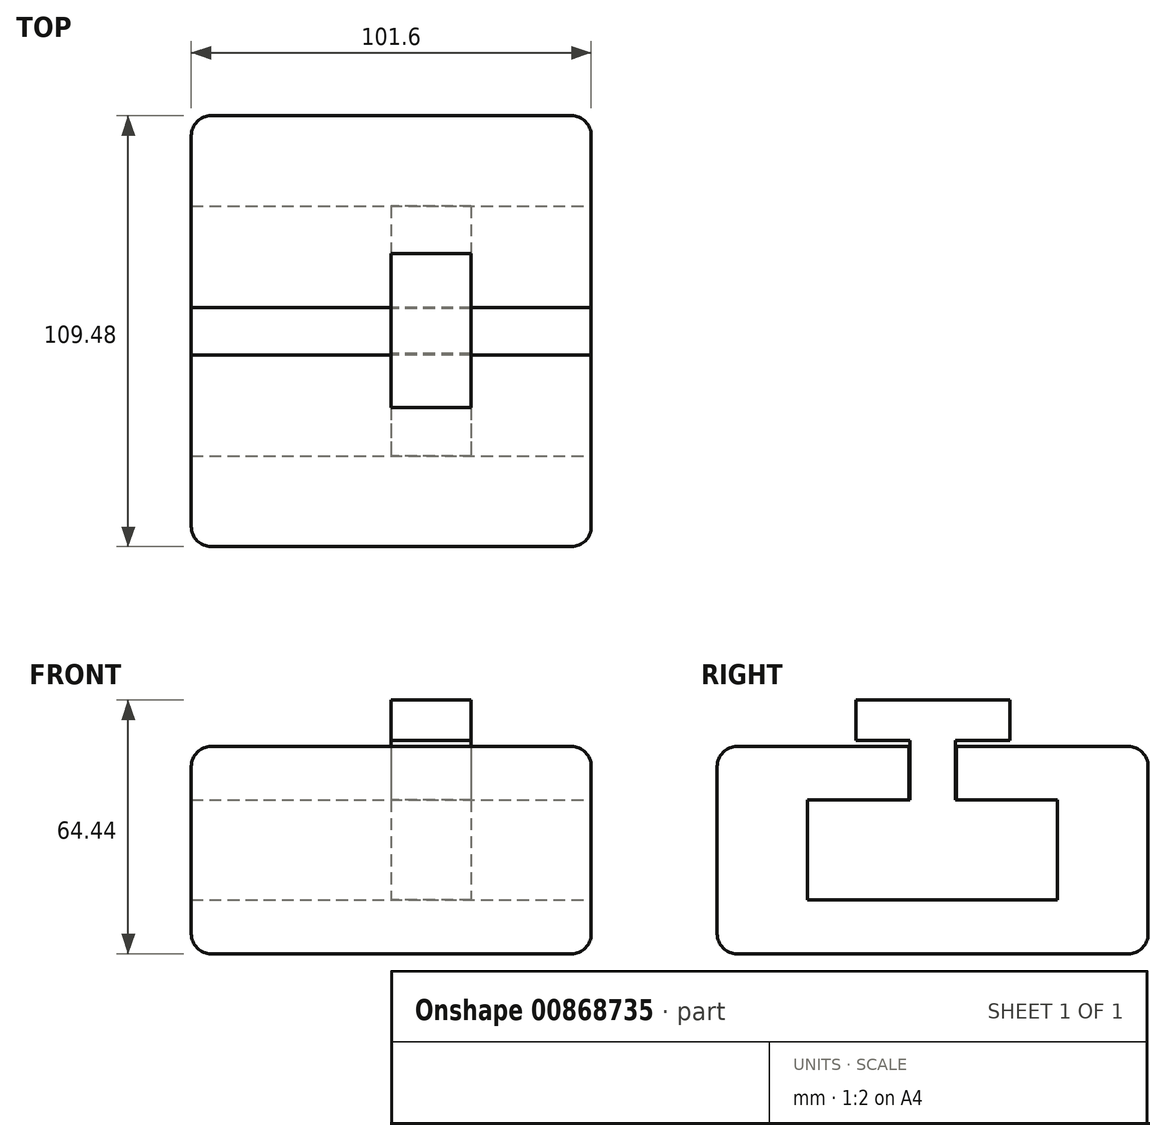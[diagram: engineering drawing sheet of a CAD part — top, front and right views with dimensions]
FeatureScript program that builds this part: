
annotation { "Feature Type Name" : "Feature", "Feature Type Description" : "" }
export const myFeature = defineFeature(function(context is Context, id is Id, definition is map)
    precondition{}
    {
        {
            var Q0;
            Q0=qCreatedBy(makeId("Right.planeOp"),FACE);
            var sketch = newSketch(context, id + "F0", { "sketchPlane" : qUnion([Q0])});
            skLineSegment(sketch, "E0.bottom", {"start": v(54.74, 26.34) * mm, "end": v(-54.74, 26.34) * mm});
            skLineSegment(sketch, "E0.top", {"start": v(54.74, -26.34) * mm, "end": v(-54.74, -26.34) * mm});
            skLineSegment(sketch, "E0.left", {"start": v(54.74, 26.34) * mm, "end": v(54.74, -26.34) * mm});
            skLineSegment(sketch, "E0.right", {"start": v(-54.74, 26.34) * mm, "end": v(-54.74, -26.34) * mm});
            skPoint(sketch, "E0.middle", {"position": v(0, 0) * mm});
            skSolve(sketch);
        }
        {
            var Q0;
            Q0 = qSketchRegion(id + "F0", true);
            extrude(context, id + "F1", {"entities" : qUnion([Q0]), "depth" : 50.8 * mm, "offsetDistance" : 25.4 * mm, "hasSecondDirection" : true, "secondDirectionOppositeDirection" : true, "secondDirectionDepth" : 50.8 * mm});
        }
        {
            var Q0;
            Q0=makeQuery(id+"F1.opExtrude","CAP_FACE",FACE,{"disambiguationData":[OSD([sQuery(id+"F0.wireOp",EDGE,"E0.bottom"),sQuery(id+"F0.wireOp",EDGE,"E0.top"),sQuery(id+"F0.wireOp",EDGE,"E0.left"),sQuery(id+"F0.wireOp",EDGE,"E0.right")])],"isStart":false});
            var sketch = newSketch(context, id + "F2", { "sketchPlane" : qUnion([Q0])});
            skLineSegment(sketch, "E1.bottom", {"start": v(31.75, 12.7) * mm, "end": v(-31.75, 12.7) * mm});
            skLineSegment(sketch, "E1.top", {"start": v(31.75, -12.7) * mm, "end": v(-31.75, -12.7) * mm});
            skLineSegment(sketch, "E1.left", {"start": v(31.75, 12.7) * mm, "end": v(31.75, -12.7) * mm});
            skLineSegment(sketch, "E1.right", {"start": v(-31.75, 12.7) * mm, "end": v(-31.75, -12.7) * mm});
            skPoint(sketch, "E1.middle", {"position": v(0, 0) * mm});
            skSolve(sketch);
        }
        {
            var Q0;
            Q0=makeQuery(id+"F2.imprint","IMPRINT",FACE,{"disambiguationData":[TD([[makeQuery(id+"F2.imprint","IMPRINT",EDGE,{"derivedFrom":sQuery(id+"F2.wireOp",EDGE,"E1.bottom")}),1.0]])]});
            extrude(context, id + "F3", {"entities" : qUnion([Q0]), "operationType" : NewBodyOperationType.REMOVE, "oppositeDirection" : true, "depth" : 124.7 * mm, "offsetDistance" : 25.4 * mm});
        }
        {
            var Q0;
            Q0=makeQuery(id+"F1.opExtrude","CAP_FACE",FACE,{"disambiguationData":[OSD([sQuery(id+"F0.wireOp",EDGE,"E0.bottom"),sQuery(id+"F0.wireOp",EDGE,"E0.top"),sQuery(id+"F0.wireOp",EDGE,"E0.left"),sQuery(id+"F0.wireOp",EDGE,"E0.right")])],"isStart":false});
            var sketch = newSketch(context, id + "F4", { "sketchPlane" : qUnion([Q0])});
            skPoint(sketch, "E2.middle", {"position": v(0, 0) * mm});
            skLineSegment(sketch, "E3.bottom", {"start": v(6.01, 30.07) * mm, "end": v(-6.01, 30.07) * mm});
            skLineSegment(sketch, "E3.top", {"start": v(6.01, 6.57) * mm, "end": v(-6.01, 6.57) * mm});
            skLineSegment(sketch, "E3.left", {"start": v(6.01, 30.07) * mm, "end": v(6.01, 6.57) * mm});
            skLineSegment(sketch, "E3.right", {"start": v(-6.01, 30.07) * mm, "end": v(-6.01, 6.57) * mm});
            skPoint(sketch, "E3.middle", {"position": v(0, 18.32) * mm});
            skSolve(sketch);
        }
        {
            var Q0;
            Q0 = qSketchRegion(id + "F4", true);
            extrude(context, id + "F5", {"entities" : qUnion([Q0]), "operationType" : NewBodyOperationType.REMOVE, "oppositeDirection" : true, "depth" : 118.87 * mm, "offsetDistance" : 25.4 * mm});
        }
        {
            var Q0;
            Q0=qCreatedBy(makeId("Right.planeOp"),FACE);
            var sketch = newSketch(context, id + "F6", { "sketchPlane" : qUnion([Q0])});
            skLineSegment(sketch, "E4.bottom", {"start": v(31.75, 12.7) * mm, "end": v(-31.75, 12.7) * mm});
            skLineSegment(sketch, "E4.top", {"start": v(31.75, -12.7) * mm, "end": v(-31.75, -12.7) * mm});
            skLineSegment(sketch, "E4.left", {"start": v(31.75, 12.7) * mm, "end": v(31.75, -12.7) * mm});
            skLineSegment(sketch, "E4.right", {"start": v(-31.75, 12.7) * mm, "end": v(-31.75, -12.7) * mm});
            skPoint(sketch, "E4.middle", {"position": v(0, 0) * mm});
            skSolve(sketch);
        }
        {
            var Q0;
            Q0 = qSketchRegion(id + "F6", true);
            extrude(context, id + "F7", {"entities" : qUnion([Q0]), "depth" : 20.32 * mm, "offsetDistance" : 25.4 * mm});
        }
        {
            var Q0;
            Q0=makeQuery(id+"F7.opExtrude","SWEPT_FACE",FACE,{"disambiguationData":[OSD([sQuery(id+"F6.wireOp",EDGE,"E4.bottom")])]});
            var sketch = newSketch(context, id + "F8", { "sketchPlane" : qUnion([Q0])});
            skLineSegment(sketch, "E5.bottom", {"start": v(20.32, 5.73) * mm, "end": v(0, 5.73) * mm});
            skLineSegment(sketch, "E5.top", {"start": v(20.32, -5.73) * mm, "end": v(0, -5.73) * mm});
            skLineSegment(sketch, "E5.left", {"start": v(20.32, 5.73) * mm, "end": v(20.32, -5.73) * mm});
            skLineSegment(sketch, "E5.right", {"start": v(0, 5.73) * mm, "end": v(0, -5.73) * mm});
            skSolve(sketch);
        }
        {
            var Q0;
            Q0 = qSketchRegion(id + "F8", true);
            extrude(context, id + "F9", {"entities" : qUnion([Q0]), "operationType" : NewBodyOperationType.ADD, "depth" : 25.4 * mm, "offsetDistance" : 25.4 * mm});
        }
        {
            var Q0;
            Q0=makeQuery(id+"F1.opExtrude","SWEPT_EDGE",EDGE,{"disambiguationData":[OSD([sQuery(id+"F0.wireOp",EDGE,"E0.bottom"),sQuery(id+"F0.wireOp",EDGE,"E0.right")])]});
            var Q1;
            Q1=makeQuery(id+"F1.opExtrude","SWEPT_EDGE",EDGE,{"disambiguationData":[OSD([sQuery(id+"F0.wireOp",EDGE,"E0.bottom"),sQuery(id+"F0.wireOp",EDGE,"E0.left")])]});
            var Q2;
            Q2=makeQuery(id+"F1.opExtrude","SWEPT_EDGE",EDGE,{"disambiguationData":[OSD([sQuery(id+"F0.wireOp",EDGE,"E0.top"),sQuery(id+"F0.wireOp",EDGE,"E0.right")])]});
            var Q3;
            Q3=makeQuery(id+"F1.opExtrude","SWEPT_EDGE",EDGE,{"disambiguationData":[OSD([sQuery(id+"F0.wireOp",EDGE,"E0.top"),sQuery(id+"F0.wireOp",EDGE,"E0.left")])]});
            var Q4;
            Q4=makeQuery(id+"F1.opExtrude","CAP_EDGE",EDGE,{"disambiguationData":[OSD([sQuery(id+"F0.wireOp",EDGE,"E0.left")])],"isStart":false});
            var Q5;
            {var subQ0=sQuery(id+"F0.wireOp",EDGE,"E0.bottom");var subQ1=sQuery(id+"F0.wireOp",EDGE,"E0.left");Q5=makeQuery(id+"F5.boolean.opBoolean","SPLIT",EDGE,{"disambiguationData":[TD([makeQuery(id+"F1.opExtrude","SWEPT_FACE",FACE,{"disambiguationData":[OSD([subQ1])]})])],"derivedFrom":makeQuery(id+"F1.opExtrude","CAP_EDGE",EDGE,{"disambiguationData":[OSD([subQ0])],"isStart":false})});}
            var Q6;
            {var subQ0=sQuery(id+"F0.wireOp",EDGE,"E0.bottom");var subQ1=sQuery(id+"F0.wireOp",EDGE,"E0.right");Q6=makeQuery(id+"F5.boolean.opBoolean","SPLIT",EDGE,{"disambiguationData":[TD([makeQuery(id+"F1.opExtrude","SWEPT_FACE",FACE,{"disambiguationData":[OSD([subQ1])]})])],"derivedFrom":makeQuery(id+"F1.opExtrude","CAP_EDGE",EDGE,{"disambiguationData":[OSD([subQ0])],"isStart":false})});}
            var Q7;
            Q7=makeQuery(id+"F1.opExtrude","CAP_EDGE",EDGE,{"disambiguationData":[OSD([sQuery(id+"F0.wireOp",EDGE,"E0.right")])],"isStart":false});
            var Q8;
            Q8=makeQuery(id+"F1.opExtrude","CAP_EDGE",EDGE,{"disambiguationData":[OSD([sQuery(id+"F0.wireOp",EDGE,"E0.top")])],"isStart":false});
            var Q9;
            {var subQ0=sQuery(id+"F0.wireOp",EDGE,"E0.bottom");var subQ1=sQuery(id+"F0.wireOp",EDGE,"E0.left");Q9=makeQuery(id+"F5.boolean.opBoolean","SPLIT",EDGE,{"disambiguationData":[TD([makeQuery(id+"F1.opExtrude","SWEPT_FACE",FACE,{"disambiguationData":[OSD([subQ1])]})])],"derivedFrom":makeQuery(id+"F1.opExtrude","CAP_EDGE",EDGE,{"disambiguationData":[OSD([subQ0])],"isStart":true})});}
            var Q10;
            {var subQ0=sQuery(id+"F0.wireOp",EDGE,"E0.bottom");var subQ1=sQuery(id+"F0.wireOp",EDGE,"E0.right");Q10=makeQuery(id+"F5.boolean.opBoolean","SPLIT",EDGE,{"disambiguationData":[TD([makeQuery(id+"F1.opExtrude","SWEPT_FACE",FACE,{"disambiguationData":[OSD([subQ1])]})])],"derivedFrom":makeQuery(id+"F1.opExtrude","CAP_EDGE",EDGE,{"disambiguationData":[OSD([subQ0])],"isStart":true})});}
            var Q11;
            Q11=makeQuery(id+"F1.opExtrude","CAP_EDGE",EDGE,{"disambiguationData":[OSD([sQuery(id+"F0.wireOp",EDGE,"E0.left")])],"isStart":true});
            var Q12;
            Q12=makeQuery(id+"F1.opExtrude","CAP_EDGE",EDGE,{"disambiguationData":[OSD([sQuery(id+"F0.wireOp",EDGE,"E0.top")])],"isStart":true});
            var Q13;
            Q13=makeQuery(id+"F1.opExtrude","CAP_EDGE",EDGE,{"disambiguationData":[OSD([sQuery(id+"F0.wireOp",EDGE,"E0.right")])],"isStart":true});
            fillet(context, id + "F10", {"entities" : qUnion([Q0, Q1, Q2, Q3, Q4, Q5, Q6, Q7, Q8, Q9, Q10, Q11, Q12, Q13]), "radius" : 5.08 * mm, "tangentPropagation" : true, "allowEdgeOverflow" : false});
        }
        {
            var Q0;
            Q0=makeQuery(id+"F9.opExtrude","SWEPT_FACE",FACE,{"disambiguationData":[OSD([sQuery(id+"F8.wireOp",EDGE,"E5.top")])]});
            var sketch = newSketch(context, id + "F11", { "sketchPlane" : qUnion([Q0])});
            skLineSegment(sketch, "E6.bottom", {"start": v(20.32, 38.1) * mm, "end": v(0, 38.1) * mm});
            skLineSegment(sketch, "E6.top", {"start": v(20.32, 27.84) * mm, "end": v(0, 27.84) * mm});
            skLineSegment(sketch, "E6.left", {"start": v(20.32, 38.1) * mm, "end": v(20.32, 27.84) * mm});
            skLineSegment(sketch, "E6.right", {"start": v(0, 38.1) * mm, "end": v(0, 27.84) * mm});
            skSolve(sketch);
        }
        {
            var Q0;
            Q0 = qSketchRegion(id + "F11", true);
            extrude(context, id + "F12", {"entities" : qUnion([Q0]), "operationType" : NewBodyOperationType.ADD, "depth" : 13.72 * mm, "offsetDistance" : 25.4 * mm, "hasSecondDirection" : true, "secondDirectionOppositeDirection" : true, "secondDirectionDepth" : 25.4 * mm});
        }
    });
